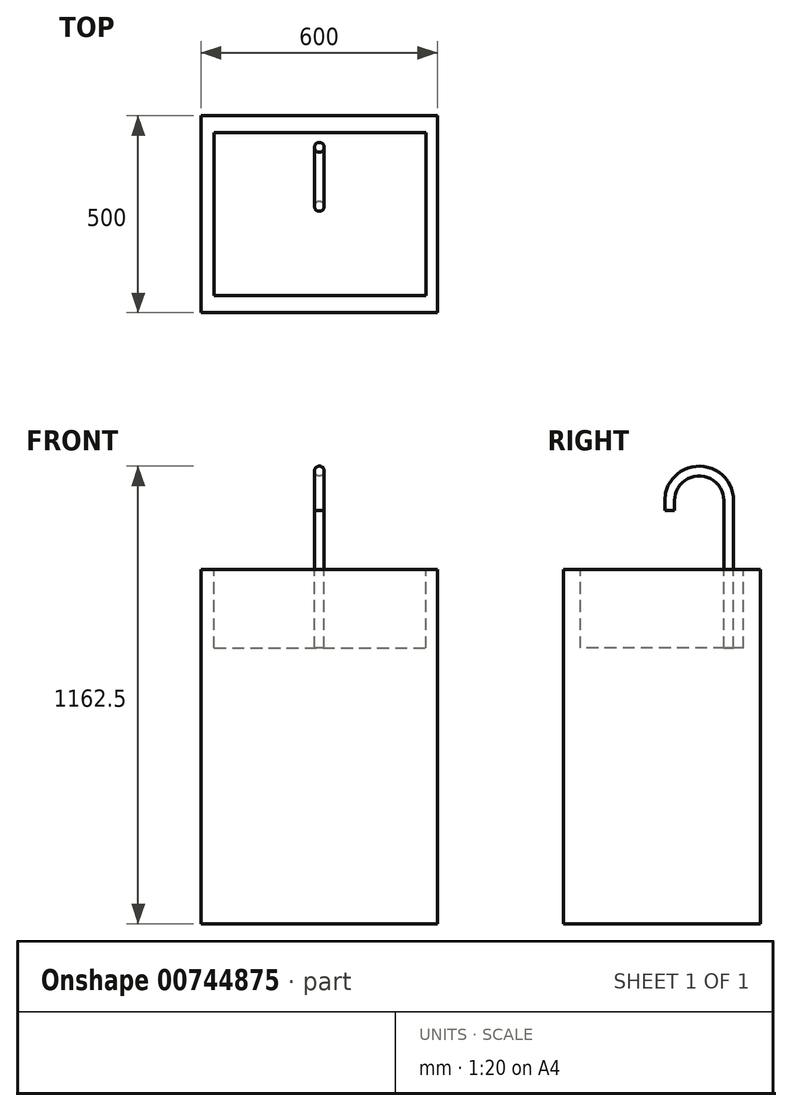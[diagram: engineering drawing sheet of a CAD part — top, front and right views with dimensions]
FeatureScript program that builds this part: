
annotation { "Feature Type Name" : "Feature", "Feature Type Description" : "" }
export const myFeature = defineFeature(function(context is Context, id is Id, definition is map)
    precondition{}
    {
        {
            var Q0;
            Q0=qCreatedBy(makeId("Top.planeOp"),FACE);
            var sketch = newSketch(context, id + "F0", { "sketchPlane" : qUnion([Q0])});
            skLineSegment(sketch, "E0.bottom", {"start": v(0, 0) * mm, "end": v(600, 0) * mm});
            skLineSegment(sketch, "E0.top", {"start": v(0, 500) * mm, "end": v(600, 500) * mm});
            skLineSegment(sketch, "E0.left", {"start": v(0, 0) * mm, "end": v(0, 500) * mm});
            skLineSegment(sketch, "E0.right", {"start": v(600, 0) * mm, "end": v(600, 500) * mm});
            skSolve(sketch);
        }
        {
            var Q0;
            Q0=makeQuery(id+"F0.imprint","IMPRINT",FACE,{"disambiguationData":[TD([[makeQuery(id+"F0.imprint","IMPRINT",EDGE,{"derivedFrom":sQuery(id+"F0.wireOp",EDGE,"E0.bottom")}),1.0]])]});
            extrude(context, id + "F1", {"entities" : qUnion([Q0]), "depth" : 900 * mm, "offsetDistance" : 25 * mm});
        }
        {
            var Q0;
            Q0=makeQuery(id+"F1.opExtrude","CAP_FACE",FACE,{"disambiguationData":[OSD([sQuery(id+"F0.wireOp",EDGE,"E0.bottom"),sQuery(id+"F0.wireOp",EDGE,"E0.top"),sQuery(id+"F0.wireOp",EDGE,"E0.left"),sQuery(id+"F0.wireOp",EDGE,"E0.right")])],"isStart":false});
            var sketch = newSketch(context, id + "F2", { "sketchPlane" : qUnion([Q0])});
            skLineSegment(sketch, "E1.bottom", {"start": v(33.06, 456.92) * mm, "end": v(570.38, 456.92) * mm});
            skLineSegment(sketch, "E1.top", {"start": v(33.06, 43.52) * mm, "end": v(570.38, 43.52) * mm});
            skLineSegment(sketch, "E1.left", {"start": v(33.06, 456.92) * mm, "end": v(33.06, 43.52) * mm});
            skLineSegment(sketch, "E1.right", {"start": v(570.38, 456.92) * mm, "end": v(570.38, 43.52) * mm});
            skSolve(sketch);
        }
        {
            var Q0;
            Q0=makeQuery(id+"F2.imprint","IMPRINT",FACE,{"disambiguationData":[TD([[makeQuery(id+"F2.imprint","IMPRINT",EDGE,{"derivedFrom":sQuery(id+"F2.wireOp",EDGE,"RxPLs1BQ-qzDJ-ytuK-W2LA-daiW1REigrPk.bottom")}),-1.0]])]});
            var Q1;
            Q1=makeQuery(id+"F2.imprint","IMPRINT",FACE,{"disambiguationData":[TD([[makeQuery(id+"F2.imprint","IMPRINT",EDGE,{"derivedFrom":sQuery(id+"F2.wireOp",EDGE,"E1.bottom")}),-1.0]])]});
            extrude(context, id + "F3", {"entities" : qUnion([Q0, Q1]), "operationType" : NewBodyOperationType.REMOVE, "oppositeDirection" : true, "depth" : 200 * mm, "offsetDistance" : 25 * mm});
        }
        {
            var Q0;
            Q0=makeQuery(id+"F1.opExtrude","SWEPT_FACE",FACE,{"disambiguationData":[OSD([sQuery(id+"F0.wireOp",EDGE,"E0.left")])]});
            var Q1;
            Q1=makeQuery(id+"F1.opExtrude","SWEPT_FACE",FACE,{"disambiguationData":[OSD([sQuery(id+"F0.wireOp",EDGE,"E0.right")])]});
            cPlane(context, id + "F4", {"entities" : qUnion([Q0, Q1]), "cplaneType" : CPlaneType.MID_PLANE, "offset" : 25 * mm, "width" : 150 * mm, "height" : 150 * mm});
        }
        {
            var Q0;
            Q0=qCreatedBy(id+"F4.planeOp",FACE);
            var sketch = newSketch(context, id + "F5", { "sketchPlane" : qUnion([Q0])});
            skLineSegment(sketch, "E2", {"start": v(-420, 589.82) * mm, "end": v(-420, 1075) * mm});
            skLineSegment(sketch, "E3", {"start": v(-345, 1150) * mm, "end": v(-345, 1150) * mm});
            skLineSegment(sketch, "E4", {"start": v(-270, 1075) * mm, "end": v(-270, 1050) * mm});
            skPoint(sketch, "E5.visualSharp", {"position": v(-270, 1150) * mm});
            skArc(sketch, "E5.filletArc", {"start": v(-270, 1075) * mm, "mid": v(-291.97, 1128.03) * mm, "end": v(-345, 1150) * mm});
            skPoint(sketch, "E6.visualSharp", {"position": v(-420, 1150) * mm});
            skArc(sketch, "E6.filletArc", {"start": v(-345, 1150) * mm, "mid": v(-398.03, 1128.03) * mm, "end": v(-420, 1075) * mm});
            skSolve(sketch);
        }
        {
            var Q0;
            Q0=makeQuery(id+"F3.boolean.opBoolean","COPY",FACE,{"derivedFrom":makeQuery(id+"F3.opExtrude","CAP_FACE",FACE,{"disambiguationData":[OSD([sQuery(id+"F2.wireOp",EDGE,"E1.bottom"),sQuery(id+"F2.wireOp",EDGE,"E1.top"),sQuery(id+"F2.wireOp",EDGE,"E1.left"),sQuery(id+"F2.wireOp",EDGE,"E1.right")])],"isStart":false})});
            var sketch = newSketch(context, id + "F6", { "sketchPlane" : qUnion([Q0])});
            skCircle(sketch, "E7", {"center": v(300, 420) * mm, "radius": 12.5 * mm});
            skSolve(sketch);
        }
        {
            var Q0;
            Q0=makeQuery(id+"F6.imprint","IMPRINT",FACE,{"disambiguationData":[TD([[makeQuery(id+"F6.imprint","IMPRINT",EDGE,{"derivedFrom":sQuery(id+"F6.wireOp",EDGE,"E7")}),1.0]])]});
            var Q1;
            Q1=sQuery(id+"F5.wireOp",EDGE,"E2");
            var Q2;
            Q2=sQuery(id+"F5.wireOp",EDGE,"E6.filletArc");
            var Q3;
            Q3=sQuery(id+"F5.wireOp",EDGE,"E5.filletArc");
            var Q4;
            Q4=sQuery(id+"F5.wireOp",EDGE,"E4");
            sweep(context, id + "F7", {"operationType" : NewBodyOperationType.ADD, "profiles" : qUnion([Q0]), "path" : qUnion([Q1, Q2, Q3, Q4])});
        }
    });
